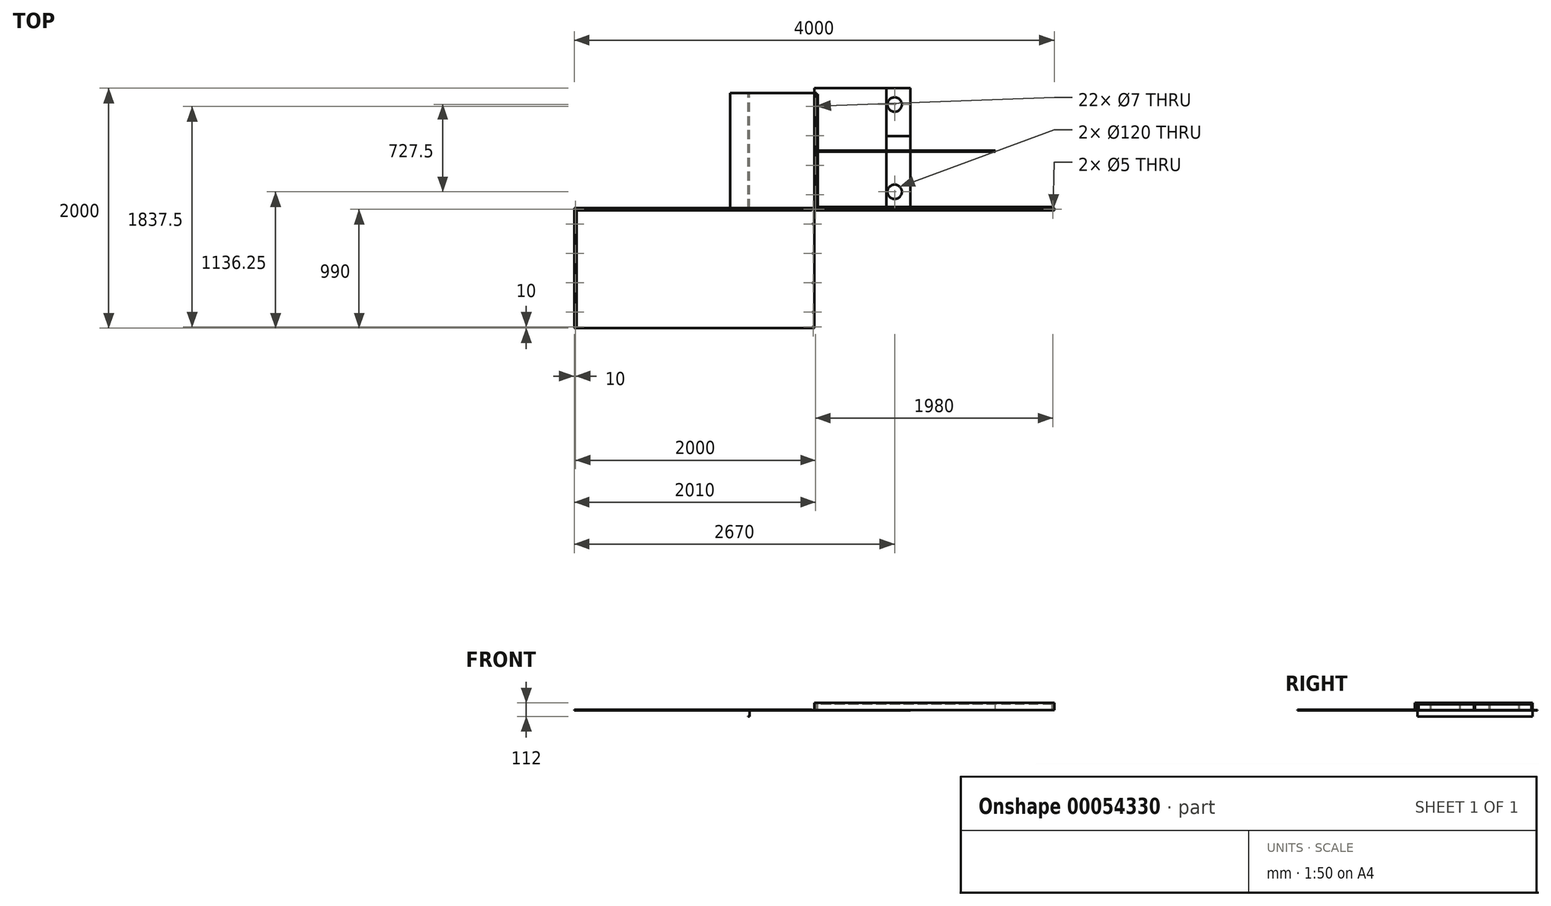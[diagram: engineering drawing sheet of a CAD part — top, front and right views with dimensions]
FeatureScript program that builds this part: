
annotation { "Feature Type Name" : "Feature", "Feature Type Description" : "" }
export const myFeature = defineFeature(function(context is Context, id is Id, definition is map)
    precondition{}
    {
        {
            var Q0;
            Q0=qCreatedBy(makeId("Top.planeOp"),FACE);
            var sketch = newSketch(context, id + "F0", { "sketchPlane" : qUnion([Q0])});
            skLineSegment(sketch, "E0.bottom", {"start": v(0, 0) * mm, "end": v(600, 0) * mm});
            skLineSegment(sketch, "E0.top", {"start": v(0, 1000) * mm, "end": v(600, 1000) * mm});
            skLineSegment(sketch, "E0.left", {"start": v(0, 0) * mm, "end": v(0, 1000) * mm});
            skLineSegment(sketch, "E0.right", {"start": v(600, 0) * mm, "end": v(600, 1000) * mm});
            skSolve(sketch);
        }
        {
            var Q0;
            Q0=makeQuery(id+"F0.imprint","IMPRINT",FACE,{"disambiguationData":[TD([[makeQuery(id+"F0.imprint","IMPRINT",EDGE,{"derivedFrom":sQuery(id+"F0.wireOp",EDGE,"E0.bottom")}),1.0]])]});
            extrude(context, id + "F1", {"entities" : qUnion([Q0]), "depth" : 3 * mm});
        }
        {
            var Q0;
            Q0=qCreatedBy(makeId("Top.planeOp"),FACE);
            var sketch = newSketch(context, id + "F2", { "sketchPlane" : qUnion([Q0])});
            skLineSegment(sketch, "E1.bottom", {"start": v(600, 0) * mm, "end": v(800, 0) * mm});
            skLineSegment(sketch, "E1.top", {"start": v(600, 600) * mm, "end": v(800, 600) * mm});
            skLineSegment(sketch, "E1.left", {"start": v(600, 0) * mm, "end": v(600, 600) * mm});
            skLineSegment(sketch, "E1.right", {"start": v(800, 0) * mm, "end": v(800, 600) * mm});
            skCircle(sketch, "E2", {"center": v(670, 136.25) * mm, "radius": 60 * mm});
            skSolve(sketch);
        }
        {
            var Q0;
            Q0=makeQuery(id+"F2.imprint","IMPRINT",FACE,{"disambiguationData":[TD([[makeQuery(id+"F2.imprint","IMPRINT",EDGE,{"derivedFrom":sQuery(id+"F2.wireOp",EDGE,"E1.bottom")}),1.0]])]});
            extrude(context, id + "F3", {"entities" : qUnion([Q0]), "depth" : 3 * mm});
        }
        {
            var Q0;
            Q0=qCreatedBy(makeId("Top.planeOp"),FACE);
            var sketch = newSketch(context, id + "F4", { "sketchPlane" : qUnion([Q0])});
            skLineSegment(sketch, "E3.bottom", {"start": v(600, 1000) * mm, "end": v(800, 1000) * mm});
            skLineSegment(sketch, "E3.top", {"start": v(600, 600) * mm, "end": v(800, 600) * mm});
            skLineSegment(sketch, "E3.left", {"start": v(600, 1000) * mm, "end": v(600, 600) * mm});
            skLineSegment(sketch, "E3.right", {"start": v(800, 1000) * mm, "end": v(800, 600) * mm});
            skCircle(sketch, "E4", {"center": v(670, 863.75) * mm, "radius": 60 * mm});
            skSolve(sketch);
        }
        {
            var Q0;
            Q0=makeQuery(id+"F4.imprint","IMPRINT",FACE,{"disambiguationData":[TD([[makeQuery(id+"F4.imprint","IMPRINT",EDGE,{"derivedFrom":sQuery(id+"F4.wireOp",EDGE,"E3.bottom")}),-1.0]])]});
            extrude(context, id + "F5", {"entities" : qUnion([Q0]), "depth" : 3 * mm});
        }
        {
            var Q0;
            Q0=qCreatedBy(makeId("Right.planeOp"),FACE);
            var sketch = newSketch(context, id + "F6", { "sketchPlane" : qUnion([Q0])});
            skLineSegment(sketch, "E5.bottom", {"start": v(-20, 3) * mm, "end": v(0, 3) * mm});
            skLineSegment(sketch, "E5.top", {"start": v(-20, 63) * mm, "end": v(0, 63) * mm});
            skLineSegment(sketch, "E5.left", {"start": v(0, 3) * mm, "end": v(0, 63) * mm});
            skLineSegment(sketch, "E5.right", {"start": v(-20, 3) * mm, "end": v(-20, 63) * mm});
            skSolve(sketch);
        }
        {
            var Q0;
            Q0=makeQuery(id+"F6.imprint","IMPRINT",FACE,{"disambiguationData":[TD([[makeQuery(id+"F6.imprint","IMPRINT",EDGE,{"derivedFrom":sQuery(id+"F6.wireOp",EDGE,"E5.bottom")}),1.0]])]});
            extrude(context, id + "F7", {"entities" : qUnion([Q0]), "depth" : 2000 * mm});
        }
        {
            var Q0;
            Q0=makeQuery(id+"F7.opExtrude","SWEPT_FACE",FACE,{"disambiguationData":[OSD([sQuery(id+"F6.wireOp",EDGE,"E5.top")])]});
            var sketch = newSketch(context, id + "F8", { "sketchPlane" : qUnion([Q0])});
            skPoint(sketch, "E6", {"position": v(10, -10) * mm});
            skPoint(sketch, "E7.1.0.0", {"position": v(1990, -10) * mm});
            skLineSegment(sketch, "E7.direction1", {"start": v(10, -10) * mm, "end": v(1990, -10) * mm, "construction": true});
            skSolve(sketch);
        }
        {
            var Q0;
            Q0=sQuery(id+"F8.wireOp",VERTEX,"E6");
            var Q1;
            Q1=sQuery(id+"F8.wireOp",VERTEX,"E7.1.0.0");
            var Q2;
            Q2=makeQuery(id+"F7.opExtrude","SWEPT_BODY",BODY,{"disambiguationData":[OSD([sQuery(id+"F6.wireOp",EDGE,"E5.bottom"),sQuery(id+"F6.wireOp",EDGE,"E5.top"),sQuery(id+"F6.wireOp",EDGE,"E5.left"),sQuery(id+"F6.wireOp",EDGE,"E5.right")])]});
            hole(context, id + "F9", {"style" : HoleStyle.SIMPLE, "holeDiameter" : 5 * mm, "endStyle" : HoleEndStyle.THROUGH, "locations" : qUnion([Q0, Q1]), "scope" : qUnion([Q2])});
        }
        {
            var Q0;
            Q0=qCreatedBy(makeId("Front.planeOp"),FACE);
            var sketch = newSketch(context, id + "F10", { "sketchPlane" : qUnion([Q0])});
            skLineSegment(sketch, "E8.bottom", {"start": v(20, 63) * mm, "end": v(0, 63) * mm});
            skLineSegment(sketch, "E8.top", {"start": v(20, 3) * mm, "end": v(0, 3) * mm});
            skLineSegment(sketch, "E8.left", {"start": v(20, 63) * mm, "end": v(20, 3) * mm});
            skLineSegment(sketch, "E8.right", {"start": v(0, 63) * mm, "end": v(0, 3) * mm});
            skSolve(sketch);
        }
        {
            var Q0;
            Q0=makeQuery(id+"F10.imprint","IMPRINT",FACE,{"disambiguationData":[TD([[makeQuery(id+"F10.imprint","IMPRINT",EDGE,{"derivedFrom":sQuery(id+"F10.wireOp",EDGE,"E8.bottom")}),1.0]])]});
            extrude(context, id + "F11", {"entities" : qUnion([Q0]), "oppositeDirection" : true, "depth" : (1000 - 40) * mm});
        }
        {
            var Q0;
            Q0=makeQuery(id+"F11.opExtrude","SWEPT_FACE",FACE,{"disambiguationData":[OSD([sQuery(id+"F10.wireOp",EDGE,"E8.bottom")])]});
            var sketch = newSketch(context, id + "F12", { "sketchPlane" : qUnion([Q0])});
            skPoint(sketch, "E9", {"position": v(10, 112.5) * mm});
            skPoint(sketch, "E10.0.1.0", {"position": v(10, 357.5) * mm});
            skPoint(sketch, "E10.0.2.0", {"position": v(10, 602.5) * mm});
            skPoint(sketch, "E10.0.3.0", {"position": v(10, 847.5) * mm});
            skLineSegment(sketch, "E10.direction1", {"start": v(10, 112.5) * mm, "end": v(35, 112.5) * mm, "construction": true});
            skLineSegment(sketch, "E10.direction2", {"start": v(10, 112.5) * mm, "end": v(10, 357.5) * mm, "construction": true});
            skSolve(sketch);
        }
        {
            var Q0;
            Q0=sQuery(id+"F12.wireOp",VERTEX,"E9");
            var Q1;
            Q1=sQuery(id+"F12.wireOp",VERTEX,"E10.0.1.0");
            var Q2;
            Q2=sQuery(id+"F12.wireOp",VERTEX,"E10.0.2.0");
            var Q3;
            Q3=sQuery(id+"F12.wireOp",VERTEX,"E10.0.3.0");
            var Q4;
            Q4=makeQuery(id+"F11.opExtrude","SWEPT_BODY",BODY,{"disambiguationData":[OSD([sQuery(id+"F10.wireOp",EDGE,"E8.bottom"),sQuery(id+"F10.wireOp",EDGE,"E8.top"),sQuery(id+"F10.wireOp",EDGE,"E8.left"),sQuery(id+"F10.wireOp",EDGE,"E8.right")])]});
            hole(context, id + "F13", {"style" : HoleStyle.SIMPLE, "holeDiameter" : 7 * mm, "endStyle" : HoleEndStyle.THROUGH, "locations" : qUnion([Q0, Q1, Q2, Q3]), "scope" : qUnion([Q4])});
        }
        {
            var Q0;
            Q0=qCreatedBy(makeId("Top.planeOp"),FACE);
            var sketch = newSketch(context, id + "F14", { "sketchPlane" : qUnion([Q0])});
            skLineSegment(sketch, "E11.bottom", {"start": v(0, 0) * mm, "end": v(-2000, 0) * mm});
            skLineSegment(sketch, "E11.top", {"start": v(0, -1000) * mm, "end": v(-2000, -1000) * mm});
            skLineSegment(sketch, "E11.left", {"start": v(0, 0) * mm, "end": v(0, -1000) * mm});
            skLineSegment(sketch, "E11.right", {"start": v(-2000, 0) * mm, "end": v(-2000, -1000) * mm});
            skSolve(sketch);
        }
        {
            var Q0;
            Q0=makeQuery(id+"F14.imprint","IMPRINT",FACE,{"disambiguationData":[TD([[makeQuery(id+"F14.imprint","IMPRINT",EDGE,{"derivedFrom":sQuery(id+"F14.wireOp",EDGE,"E11.bottom")}),1.0]])]});
            extrude(context, id + "F15", {"entities" : qUnion([Q0]), "depth" : 3 * mm});
        }
        {
            var Q0;
            Q0=makeQuery(id+"F15.opExtrude","CAP_FACE",FACE,{"disambiguationData":[OSD([sQuery(id+"F14.wireOp",EDGE,"E11.bottom"),sQuery(id+"F14.wireOp",EDGE,"E11.top"),sQuery(id+"F14.wireOp",EDGE,"E11.left"),sQuery(id+"F14.wireOp",EDGE,"E11.right")])],"isStart":false});
            var sketch = newSketch(context, id + "F16", { "sketchPlane" : qUnion([Q0])});
            skPoint(sketch, "E12", {"position": v(-1990, -990) * mm});
            skPoint(sketch, "E13.0.1.0", {"position": v(-1990, -10) * mm});
            skPoint(sketch, "E13.1.0.0", {"position": v(-10, -990) * mm});
            skPoint(sketch, "E13.1.1.0", {"position": v(-10, -10) * mm});
            skLineSegment(sketch, "E13.direction1", {"start": v(-1990, -990) * mm, "end": v(-10, -990) * mm, "construction": true});
            skLineSegment(sketch, "E13.direction2", {"start": v(-1990, -990) * mm, "end": v(-1990, -10) * mm, "construction": true});
            skPoint(sketch, "E14", {"position": v(-1990, -867.5) * mm});
            skPoint(sketch, "E15.0.1.0", {"position": v(-1990, -622.5) * mm});
            skPoint(sketch, "E15.0.2.0", {"position": v(-1990, -377.5) * mm});
            skPoint(sketch, "E15.0.3.0", {"position": v(-1990, -132.5) * mm});
            skLineSegment(sketch, "E15.direction1", {"start": v(-1990, -867.5) * mm, "end": v(-10, -867.5) * mm, "construction": true});
            skLineSegment(sketch, "E15.direction2", {"start": v(-1990, -867.5) * mm, "end": v(-1990, -622.5) * mm, "construction": true});
            skPoint(sketch, "E16.0.1.0", {"position": v(-10, -867.5) * mm});
            skPoint(sketch, "E16.0.1.1", {"position": v(-10, -622.5) * mm});
            skPoint(sketch, "E16.0.1.2", {"position": v(-10, -377.5) * mm});
            skPoint(sketch, "E16.0.1.3", {"position": v(-10, -132.5) * mm});
            skSolve(sketch);
        }
        {
            var Q0;
            Q0=sQuery(id+"F16.wireOp",VERTEX,"E12");
            var Q1;
            Q1=sQuery(id+"F16.wireOp",VERTEX,"E14");
            var Q2;
            Q2=sQuery(id+"F16.wireOp",VERTEX,"E15.0.1.0");
            var Q3;
            Q3=sQuery(id+"F16.wireOp",VERTEX,"E15.0.2.0");
            var Q4;
            Q4=sQuery(id+"F16.wireOp",VERTEX,"E15.0.3.0");
            var Q5;
            Q5=sQuery(id+"F16.wireOp",VERTEX,"E13.0.1.0");
            var Q6;
            Q6=sQuery(id+"F16.wireOp",VERTEX,"E13.1.1.0");
            var Q7;
            Q7=sQuery(id+"F16.wireOp",VERTEX,"E13.1.0.0");
            var Q8;
            Q8=sQuery(id+"F16.wireOp",VERTEX,"E16.0.1.0");
            var Q9;
            Q9=sQuery(id+"F16.wireOp",VERTEX,"E16.0.1.1");
            var Q10;
            Q10=sQuery(id+"F16.wireOp",VERTEX,"E16.0.1.2");
            var Q11;
            Q11=sQuery(id+"F16.wireOp",VERTEX,"E16.0.1.3");
            var Q12;
            Q12=makeQuery(id+"F15.opExtrude","SWEPT_BODY",BODY,{"disambiguationData":[OSD([sQuery(id+"F14.wireOp",EDGE,"E11.bottom"),sQuery(id+"F14.wireOp",EDGE,"E11.top"),sQuery(id+"F14.wireOp",EDGE,"E11.left"),sQuery(id+"F14.wireOp",EDGE,"E11.right")])]});
            hole(context, id + "F17", {"style" : HoleStyle.SIMPLE, "holeDiameter" : 7 * mm, "endStyle" : HoleEndStyle.THROUGH, "locations" : qUnion([Q0, Q1, Q2, Q3, Q4, Q5, Q6, Q7, Q8, Q9, Q10, Q11]), "scope" : qUnion([Q12])});
        }
        {
            var Q0;
            Q0=makeQuery(id+"F11.opExtrude","SWEPT_FACE",FACE,{"disambiguationData":[OSD([sQuery(id+"F10.wireOp",EDGE,"E8.left")])]});
            var sketch = newSketch(context, id + "F18", { "sketchPlane" : qUnion([Q0])});
            skLineSegment(sketch, "E17.bottom", {"start": v(0, 3) * mm, "end": v(10, 3) * mm});
            skLineSegment(sketch, "E17.top", {"start": v(0, 53) * mm, "end": v(10, 53) * mm});
            skLineSegment(sketch, "E17.left", {"start": v(0, 3) * mm, "end": v(0, 53) * mm});
            skLineSegment(sketch, "E17.right", {"start": v(10, 3) * mm, "end": v(10, 53) * mm});
            skSolve(sketch);
        }
        {
            var Q0;
            Q0=makeQuery(id+"F18.imprint","IMPRINT",FACE,{"disambiguationData":[TD([[makeQuery(id+"F18.imprint","IMPRINT",EDGE,{"derivedFrom":sQuery(id+"F18.wireOp",EDGE,"E17.bottom")}),-1.0]])]});
            extrude(context, id + "F19", {"entities" : qUnion([Q0]), "depth" : (2000 - 40) * mm});
        }
        {
            var Q0;
            Q0=makeQuery(id+"F19.opExtrude","SWEPT_FACE",FACE,{"disambiguationData":[OSD([sQuery(id+"F18.wireOp",EDGE,"E17.right")])]});
            var sketch = newSketch(context, id + "F20", { "sketchPlane" : qUnion([Q0])});
            skLineSegment(sketch, "E18.bottom", {"start": v(-20, 3) * mm, "end": v(-30, 3) * mm});
            skLineSegment(sketch, "E18.top", {"start": v(-20, 53) * mm, "end": v(-30, 53) * mm});
            skLineSegment(sketch, "E18.left", {"start": v(-20, 3) * mm, "end": v(-20, 53) * mm});
            skLineSegment(sketch, "E18.right", {"start": v(-30, 3) * mm, "end": v(-30, 53) * mm});
            skSolve(sketch);
        }
        {
            var Q0;
            Q0=makeQuery(id+"F20.imprint","IMPRINT",FACE,{"disambiguationData":[TD([[makeQuery(id+"F20.imprint","IMPRINT",EDGE,{"derivedFrom":sQuery(id+"F20.wireOp",EDGE,"E18.bottom")}),1.0]])]});
            extrude(context, id + "F21", {"entities" : qUnion([Q0]), "depth" : 940 * mm});
        }
        {
            var Q0;
            Q0=makeQuery(id+"F21.opExtrude","SWEPT_FACE",FACE,{"disambiguationData":[OSD([sQuery(id+"F20.wireOp",EDGE,"E18.right")])]});
            var sketch = newSketch(context, id + "F22", { "sketchPlane" : qUnion([Q0])});
            skLineSegment(sketch, "E19.bottom", {"start": v(470, 3) * mm, "end": v(480, 3) * mm});
            skLineSegment(sketch, "E19.top", {"start": v(470, 53) * mm, "end": v(480, 53) * mm});
            skLineSegment(sketch, "E19.left", {"start": v(470, 3) * mm, "end": v(470, 53) * mm});
            skLineSegment(sketch, "E19.right", {"start": v(480, 3) * mm, "end": v(480, 53) * mm});
            skSolve(sketch);
        }
        {
            var Q0;
            Q0=makeQuery(id+"F22.imprint","IMPRINT",FACE,{"disambiguationData":[TD([[makeQuery(id+"F22.imprint","IMPRINT",EDGE,{"derivedFrom":sQuery(id+"F22.wireOp",EDGE,"E19.bottom")}),-1.0]])]});
            extrude(context, id + "F23", {"entities" : qUnion([Q0]), "depth" : 1480 * mm});
        }
        {
            var Q0;
            Q0=makeQuery(id+"F15.opExtrude","CAP_FACE",FACE,{"disambiguationData":[OSD([sQuery(id+"F14.wireOp",EDGE,"E11.bottom"),sQuery(id+"F14.wireOp",EDGE,"E11.top"),sQuery(id+"F14.wireOp",EDGE,"E11.left"),sQuery(id+"F14.wireOp",EDGE,"E11.right")])],"isStart":false});
            var sketch = newSketch(context, id + "F24", { "sketchPlane" : qUnion([Q0])});
            skLineSegment(sketch, "E20.bottom", {"start": v(-2000, 0) * mm, "end": v(0, 0) * mm});
            skLineSegment(sketch, "E20.top", {"start": v(-2000, -1000) * mm, "end": v(0, -1000) * mm});
            skLineSegment(sketch, "E20.left", {"start": v(-2000, 0) * mm, "end": v(-2000, -1000) * mm});
            skLineSegment(sketch, "E20.right", {"start": v(0, 0) * mm, "end": v(0, -1000) * mm});
            skLineSegment(sketch, "E21.bottom", {"start": v(-20, -20) * mm, "end": v(-1980, -20) * mm});
            skLineSegment(sketch, "E21.top", {"start": v(-20, -980) * mm, "end": v(-1980, -980) * mm});
            skLineSegment(sketch, "E21.left", {"start": v(-20, -20) * mm, "end": v(-20, -980) * mm});
            skLineSegment(sketch, "E21.right", {"start": v(-1980, -20) * mm, "end": v(-1980, -980) * mm});
            skLineSegment(sketch, "E22", {"start": v(-1980, -20) * mm, "end": v(-1980, 0) * mm});
            skLineSegment(sketch, "E23", {"start": v(-1980, -980) * mm, "end": v(-1980, -1000) * mm});
            skLineSegment(sketch, "E24", {"start": v(-20, -20) * mm, "end": v(-20, 0) * mm});
            skLineSegment(sketch, "E25", {"start": v(-20, -980) * mm, "end": v(-20, -1000) * mm});
            skSolve(sketch);
        }
        {
            var Q0;
            Q0=makeQuery(id+"F24.imprint","IMPRINT",FACE,{"disambiguationData":[TD([[makeQuery(id+"F24.imprint","IMPRINT",EDGE,{"derivedFrom":sQuery(id+"F24.wireOp",EDGE,"E20.bottom")}),1.0]])]});
            extrude(context, id + "F25", {"entities" : qUnion([Q0]), "depth" : 5 * mm});
        }
        {
            var Q0;
            {var subQ2=sQuery(id+"F24.wireOp",EDGE,"E20.left");Q0=makeQuery(id+"F24.imprint","IMPRINT",FACE,{"disambiguationData":[TD([[makeQuery(id+"F24.imprint","IMPRINT",EDGE,{"derivedFrom":subQ2}),1.0]])]});}
            var Q1;
            Q1=makeQuery(id+"F24.imprint","IMPRINT",FACE,{"disambiguationData":[TD([[makeQuery(id+"F24.imprint","IMPRINT",EDGE,{"derivedFrom":makeQuery(id+"F17.hole-5.boolean.opBoolean","COPY",EDGE,{"derivedFrom":makeQuery(id+"F17.hole-5.opRevolve","SWEPT_EDGE",EDGE,{"disambiguationData":[OSD([sQuery(id+"F17.hole-5.sketch.wireOp",EDGE,"core_line_2"),sQuery(id+"F17.hole-5.sketch.wireOp",EDGE,"core_line_3")])]})})}),1.0]])]});
            var Q2;
            Q2=makeQuery(id+"F24.imprint","IMPRINT",FACE,{"disambiguationData":[TD([[makeQuery(id+"F24.imprint","IMPRINT",EDGE,{"derivedFrom":makeQuery(id+"F17.hole-4.boolean.opBoolean","COPY",EDGE,{"derivedFrom":makeQuery(id+"F17.hole-4.opRevolve","SWEPT_EDGE",EDGE,{"disambiguationData":[OSD([sQuery(id+"F17.hole-4.sketch.wireOp",EDGE,"core_line_2"),sQuery(id+"F17.hole-4.sketch.wireOp",EDGE,"core_line_3")])]})})}),1.0]])]});
            var Q3;
            Q3=makeQuery(id+"F24.imprint","IMPRINT",FACE,{"disambiguationData":[TD([[makeQuery(id+"F24.imprint","IMPRINT",EDGE,{"derivedFrom":makeQuery(id+"F17.hole-3.boolean.opBoolean","COPY",EDGE,{"derivedFrom":makeQuery(id+"F17.hole-3.opRevolve","SWEPT_EDGE",EDGE,{"disambiguationData":[OSD([sQuery(id+"F17.hole-3.sketch.wireOp",EDGE,"core_line_2"),sQuery(id+"F17.hole-3.sketch.wireOp",EDGE,"core_line_3")])]})})}),1.0]])]});
            var Q4;
            Q4=makeQuery(id+"F24.imprint","IMPRINT",FACE,{"disambiguationData":[TD([[makeQuery(id+"F24.imprint","IMPRINT",EDGE,{"derivedFrom":makeQuery(id+"F17.hole-2.boolean.opBoolean","COPY",EDGE,{"derivedFrom":makeQuery(id+"F17.hole-2.opRevolve","SWEPT_EDGE",EDGE,{"disambiguationData":[OSD([sQuery(id+"F17.hole-2.sketch.wireOp",EDGE,"core_line_2"),sQuery(id+"F17.hole-2.sketch.wireOp",EDGE,"core_line_3")])]})})}),1.0]])]});
            var Q5;
            Q5=makeQuery(id+"F24.imprint","IMPRINT",FACE,{"disambiguationData":[TD([[makeQuery(id+"F24.imprint","IMPRINT",EDGE,{"derivedFrom":makeQuery(id+"F17.hole-1.boolean.opBoolean","COPY",EDGE,{"derivedFrom":makeQuery(id+"F17.hole-1.opRevolve","SWEPT_EDGE",EDGE,{"disambiguationData":[OSD([sQuery(id+"F17.hole-1.sketch.wireOp",EDGE,"core_line_2"),sQuery(id+"F17.hole-1.sketch.wireOp",EDGE,"core_line_3")])]})})}),1.0]])]});
            var Q6;
            Q6=makeQuery(id+"F24.imprint","IMPRINT",FACE,{"disambiguationData":[TD([[makeQuery(id+"F24.imprint","IMPRINT",EDGE,{"derivedFrom":makeQuery(id+"F17.hole-0.boolean.opBoolean","COPY",EDGE,{"derivedFrom":makeQuery(id+"F17.hole-0.opRevolve","SWEPT_EDGE",EDGE,{"disambiguationData":[OSD([sQuery(id+"F17.hole-0.sketch.wireOp",EDGE,"core_line_2"),sQuery(id+"F17.hole-0.sketch.wireOp",EDGE,"core_line_3")])]})})}),1.0]])]});
            extrude(context, id + "F26", {"entities" : qUnion([Q0, Q1, Q2, Q3, Q4, Q5, Q6]), "depth" : 5 * mm});
        }
        {
            var Q0;
            Q0=qCreatedBy(makeId("Top.planeOp"),FACE);
            var sketch = newSketch(context, id + "F27", { "sketchPlane" : qUnion([Q0])});
            skLineSegment(sketch, "E26.bottom", {"start": v(0, 0) * mm, "end": v(-540, 0) * mm});
            skLineSegment(sketch, "E26.top", {"start": v(0, 960) * mm, "end": v(-540, 960) * mm});
            skLineSegment(sketch, "E26.left", {"start": v(0, 0) * mm, "end": v(0, 960) * mm});
            skLineSegment(sketch, "E26.right", {"start": v(-540, 0) * mm, "end": v(-540, 960) * mm});
            skLineSegment(sketch, "E27.bottom", {"start": v(-540, 0) * mm, "end": v(-700, 0) * mm});
            skLineSegment(sketch, "E27.top", {"start": v(-540, 960) * mm, "end": v(-700, 960) * mm});
            skLineSegment(sketch, "E27.right", {"start": v(-700, 0) * mm, "end": v(-700, 960) * mm});
            skSolve(sketch);
        }
        {
            var Q0;
            Q0=makeQuery(id+"F27.imprint","IMPRINT",FACE,{"disambiguationData":[TD([[makeQuery(id+"F27.imprint","IMPRINT",EDGE,{"derivedFrom":sQuery(id+"F27.wireOp",EDGE,"E26.bottom")}),-1.0]])]});
            extrude(context, id + "F28", {"entities" : qUnion([Q0]), "depth" : 1 * mm});
        }
        {
            var Q0;
            Q0=makeQuery(id+"F27.imprint","IMPRINT",FACE,{"disambiguationData":[TD([[makeQuery(id+"F27.imprint","IMPRINT",EDGE,{"derivedFrom":sQuery(id+"F27.wireOp",EDGE,"E27.bottom")}),-1.0]])]});
            extrude(context, id + "F29", {"entities" : qUnion([Q0]), "depth" : 1 * mm});
        }
        {
            var Q0;
            Q0=makeQuery(id+"F28.opExtrude","SWEPT_FACE",FACE,{"disambiguationData":[OSD([sQuery(id+"F27.wireOp",EDGE,"E26.top")])]});
            var sketch = newSketch(context, id + "F30", { "sketchPlane" : qUnion([Q0])});
            skLineSegment(sketch, "E28", {"start": v(540, 0) * mm, "end": v(540, -48) * mm});
            skLineSegment(sketch, "E29", {"start": v(540, -48) * mm, "end": v(550, -48) * mm});
            skLineSegment(sketch, "E30", {"start": v(550, -48) * mm, "end": v(550, -49) * mm});
            skLineSegment(sketch, "E31", {"start": v(550, -49) * mm, "end": v(539, -49) * mm});
            skLineSegment(sketch, "E32", {"start": v(539, -49) * mm, "end": v(539, 0) * mm});
            skSolve(sketch);
        }
        {
            var Q0;
            {var subQ0=sQuery(id+"F30.wireOp",EDGE,"E28");Q0=makeQuery(id+"F30.imprint","IMPRINT",FACE,{"disambiguationData":[TD([[makeQuery(id+"F30.imprint","IMPRINT",EDGE,{"derivedFrom":subQ0}),-1.0]])]});}
            var Q1;
            Q1=makeQuery(id+"F28.opExtrude","SWEPT_FACE",FACE,{"disambiguationData":[OSD([sQuery(id+"F27.wireOp",EDGE,"E26.bottom")])]});
            extrude(context, id + "F31", {"entities" : qUnion([Q0]), "operationType" : NewBodyOperationType.ADD, "endBound" : BoundingType.UP_TO_SURFACE, "oppositeDirection" : true, "endBoundEntityFace" : qUnion([Q1]), "depth" : 25 * mm});
        }
    });
